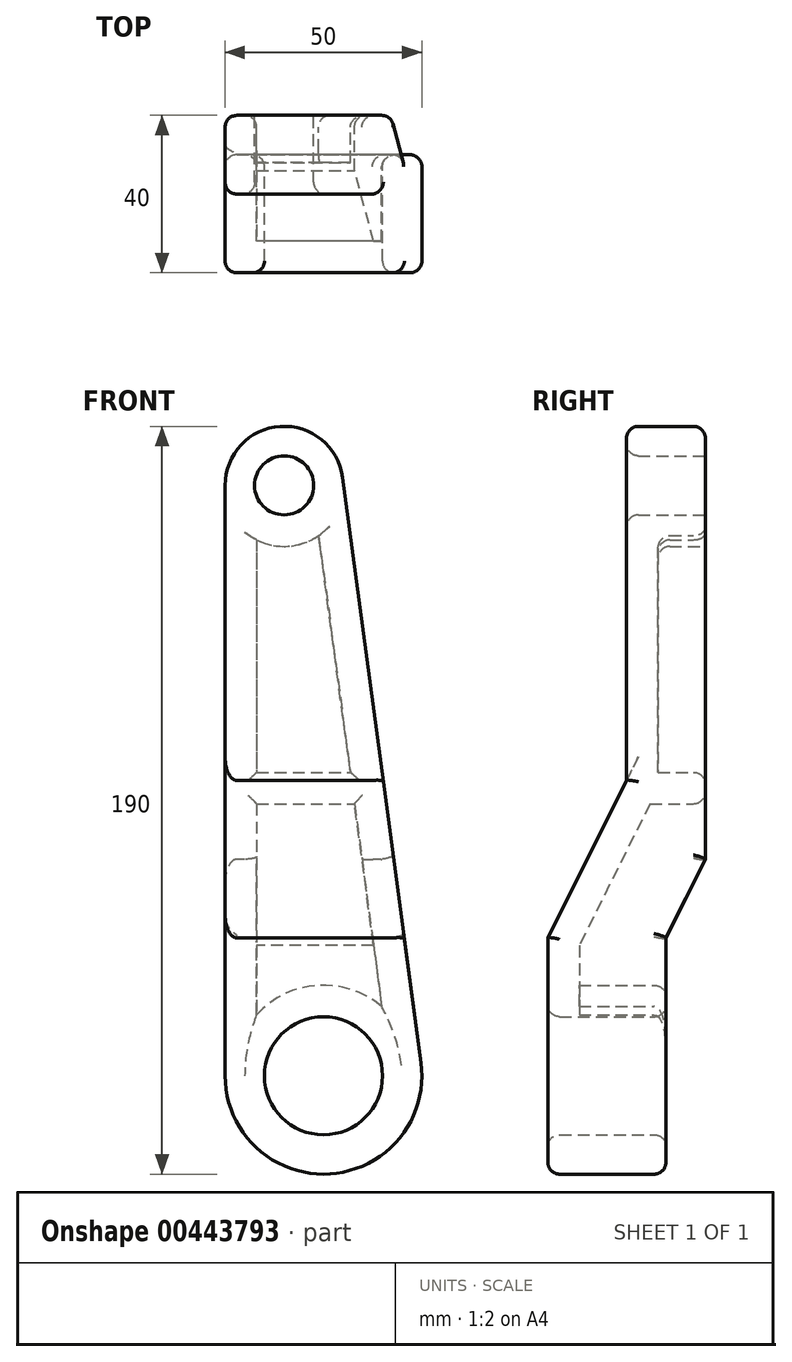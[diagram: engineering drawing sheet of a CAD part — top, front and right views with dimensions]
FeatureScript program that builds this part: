
annotation { "Feature Type Name" : "Feature", "Feature Type Description" : "" }
export const myFeature = defineFeature(function(context is Context, id is Id, definition is map)
    precondition{}
    {
        {
            var Q0;
            Q0=qCreatedBy(makeId("Front.planeOp"),FACE);
            var sketch = newSketch(context, id + "F0", { "sketchPlane" : qUnion([Q0])});
            skArc(sketch, "E0", {"start": v(-25, 0) * mm, "mid": v(1.66, -24.94) * mm, "end": v(24.78, 3.32) * mm});
            skArc(sketch, "E1", {"start": v(4.87, 152) * mm, "mid": v(-11, 164.97) * mm, "end": v(-25, 150) * mm});
            skLineSegment(sketch, "E2", {"start": v(-25, 150) * mm, "end": v(-25, 0) * mm});
            skLineSegment(sketch, "E3", {"start": v(4.87, 152) * mm, "end": v(24.78, 3.32) * mm});
            skSolve(sketch);
        }
        {
            var Q0;
            Q0 = qSketchRegion(id + "F0", true);
            extrude(context, id + "F1", {"entities" : qUnion([Q0]), "depth" : 40 * mm});
        }
        {
            var Q0;
            Q0=makeQuery(id+"F1.opExtrude","SWEPT_FACE",FACE,{"disambiguationData":[OSD([sQuery(id+"F0.wireOp",EDGE,"E2")])]});
            var sketch = newSketch(context, id + "F2", { "sketchPlane" : qUnion([Q0])});
            skLineSegment(sketch, "E4", {"start": v(0, 55) * mm, "end": v(0, -25.94) * mm});
            skLineSegment(sketch, "E5", {"start": v(10, -25.94) * mm, "end": v(10, 35) * mm});
            skLineSegment(sketch, "E6", {"start": v(10, 35) * mm, "end": v(0, 55) * mm});
            skLineSegment(sketch, "E7", {"start": v(40, 35) * mm, "end": v(40, 165.97) * mm});
            skLineSegment(sketch, "E8", {"start": v(20, 165.97) * mm, "end": v(20, 75) * mm});
            skLineSegment(sketch, "E9", {"start": v(20, 75) * mm, "end": v(40, 35) * mm});
            skLineSegment(sketch, "E10", {"start": v(0, -25.94) * mm, "end": v(10, -25.94) * mm});
            skLineSegment(sketch, "E11", {"start": v(20, 165.97) * mm, "end": v(40, 165.97) * mm});
            skSolve(sketch);
        }
        {
            var Q0;
            Q0 = qSketchRegion(id + "F2", true);
            extrude(context, id + "F3", {"entities" : qUnion([Q0]), "operationType" : NewBodyOperationType.REMOVE, "endBound" : BoundingType.THROUGH_ALL, "oppositeDirection" : true, "depth" : 25 * mm});
        }
        {
            var Q0;
            Q0=makeQuery(id+"F1.opExtrude","CAP_FACE",FACE,{"disambiguationData":[OSD([sQuery(id+"F0.wireOp",EDGE,"E0"),sQuery(id+"F0.wireOp",EDGE,"E1"),sQuery(id+"F0.wireOp",EDGE,"E2"),sQuery(id+"F0.wireOp",EDGE,"E3")])],"isStart":true});
            var sketch = newSketch(context, id + "F4", { "sketchPlane" : qUnion([Q0])});
            skCircle(sketch, "E12", {"center": v(10, 150) * mm, "radius": 7.5 * mm});
            skCircle(sketch, "E13", {"center": v(0, 0) * mm, "radius": 15 * mm});
            skSolve(sketch);
        }
        {
            var Q0;
            Q0 = qSketchRegion(id + "F4", true);
            extrude(context, id + "F5", {"entities" : qUnion([Q0]), "operationType" : NewBodyOperationType.REMOVE, "endBound" : BoundingType.THROUGH_ALL, "oppositeDirection" : true, "depth" : 25 * mm});
        }
        {
            var Q0;
            Q0=makeQuery(id+"F1.opExtrude","CAP_FACE",FACE,{"disambiguationData":[OSD([sQuery(id+"F0.wireOp",EDGE,"E0"),sQuery(id+"F0.wireOp",EDGE,"E1"),sQuery(id+"F0.wireOp",EDGE,"E2"),sQuery(id+"F0.wireOp",EDGE,"E3")])],"isStart":true});
            var Q1;
            Q1=makeQuery(id+"F3.boolean.opBoolean","COPY",FACE,{"derivedFrom":makeQuery(id+"F3.opExtrude","SWEPT_FACE",FACE,{"disambiguationData":[OSD([sQuery(id+"F2.wireOp",EDGE,"E6")])]})});
            var Q2;
            Q2=makeQuery(id+"F3.boolean.opBoolean","COPY",FACE,{"derivedFrom":makeQuery(id+"F3.opExtrude","SWEPT_FACE",FACE,{"disambiguationData":[OSD([sQuery(id+"F2.wireOp",EDGE,"E5")])]})});
            shell(context, id + "F6", {"entities" : qUnion([Q0, Q1, Q2]), "thickness" : 8 * mm});
        }
        {
            var Q0;
            Q0=makeQuery(id+"F1.opExtrude","CAP_FACE",FACE,{"disambiguationData":[OSD([sQuery(id+"F0.wireOp",EDGE,"E0"),sQuery(id+"F0.wireOp",EDGE,"E1"),sQuery(id+"F0.wireOp",EDGE,"E2"),sQuery(id+"F0.wireOp",EDGE,"E3")])],"isStart":true});
            var sketch = newSketch(context, id + "F7", { "sketchPlane" : qUnion([Q0])});
            skLineSegment(sketch, "E14", {"start": v(-6.82, 77.11) * mm, "end": v(17, 77.11) * mm});
            skLineSegment(sketch, "E15", {"start": v(-7.9, 69.11) * mm, "end": v(17, 69.11) * mm});
            skLineSegment(sketch, "E16.0", {"start": v(1.23, 137.22) * mm, "end": v(-9.79, 55) * mm});
            skLineSegment(sketch, "E17.0", {"start": v(17, 136.17) * mm, "end": v(17, 55) * mm});
            skSolve(sketch);
        }
        {
            var Q0;
            Q0 = qSketchRegion(id + "F7", true);
            extrude(context, id + "F8", {"entities" : qUnion([Q0]), "operationType" : NewBodyOperationType.ADD, "endBound" : BoundingType.UP_TO_NEXT, "oppositeDirection" : true, "depth" : 25 * mm});
        }
        {
            var Q0;
            Q0=makeQuery(id+"F3.boolean.opBoolean","INTERSECT",EDGE,{"derivedFrom":[makeQuery(id+"F1.opExtrude","SWEPT_FACE",FACE,{"disambiguationData":[OSD([sQuery(id+"F0.wireOp",EDGE,"E3")])]}),makeQuery(id+"F3.opExtrude","SWEPT_FACE",FACE,{"disambiguationData":[OSD([sQuery(id+"F2.wireOp",EDGE,"E8")])]})]});
            var Q1;
            Q1=makeQuery(id+"F1.opExtrude","CAP_EDGE",EDGE,{"disambiguationData":[OSD([sQuery(id+"F0.wireOp",EDGE,"E3")])],"isStart":true});
            var Q2;
            Q2=makeQuery(id+"F1.opExtrude","CAP_EDGE",EDGE,{"disambiguationData":[OSD([sQuery(id+"F0.wireOp",EDGE,"E1")])],"isStart":true});
            var Q3;
            Q3=makeQuery(id+"F3.boolean.opBoolean","INTERSECT",EDGE,{"derivedFrom":[makeQuery(id+"F1.opExtrude","SWEPT_FACE",FACE,{"disambiguationData":[OSD([sQuery(id+"F0.wireOp",EDGE,"E1")])]}),makeQuery(id+"F3.opExtrude","SWEPT_FACE",FACE,{"disambiguationData":[OSD([sQuery(id+"F2.wireOp",EDGE,"E8")])]})]});
            var Q4;
            Q4=makeQuery(id+"F3.boolean.opBoolean","INTERSECT",EDGE,{"derivedFrom":[makeQuery(id+"F1.opExtrude","SWEPT_FACE",FACE,{"disambiguationData":[OSD([sQuery(id+"F0.wireOp",EDGE,"E3")])]}),makeQuery(id+"F3.opExtrude","SWEPT_FACE",FACE,{"disambiguationData":[OSD([sQuery(id+"F2.wireOp",EDGE,"E9")])]})]});
            var Q5;
            Q5=makeQuery(id+"F1.opExtrude","CAP_EDGE",EDGE,{"disambiguationData":[OSD([sQuery(id+"F0.wireOp",EDGE,"E3")])],"isStart":false});
            var Q6;
            Q6=makeQuery(id+"F1.opExtrude","CAP_EDGE",EDGE,{"disambiguationData":[OSD([sQuery(id+"F0.wireOp",EDGE,"E0")])],"isStart":false});
            var Q7;
            Q7=makeQuery(id+"F1.opExtrude","CAP_EDGE",EDGE,{"disambiguationData":[OSD([sQuery(id+"F0.wireOp",EDGE,"E2")])],"isStart":false});
            var Q8;
            Q8=makeQuery(id+"F3.boolean.opBoolean","COPY",EDGE,{"derivedFrom":makeQuery(id+"F3.opExtrude","CAP_EDGE",EDGE,{"disambiguationData":[OSD([sQuery(id+"F2.wireOp",EDGE,"E9")])],"isStart":true})});
            var Q9;
            Q9=makeQuery(id+"F3.boolean.opBoolean","COPY",EDGE,{"derivedFrom":makeQuery(id+"F3.opExtrude","CAP_EDGE",EDGE,{"disambiguationData":[OSD([sQuery(id+"F2.wireOp",EDGE,"E8")])],"isStart":true})});
            var Q10;
            Q10=makeQuery(id+"F5.boolean.opBoolean","INTERSECT",EDGE,{"derivedFrom":[makeQuery(id+"F3.boolean.opBoolean","COPY",FACE,{"derivedFrom":makeQuery(id+"F3.opExtrude","SWEPT_FACE",FACE,{"disambiguationData":[OSD([sQuery(id+"F2.wireOp",EDGE,"E8")])]})}),makeQuery(id+"F5.opExtrude","SWEPT_FACE",FACE,{"disambiguationData":[OSD([sQuery(id+"F4.wireOp",EDGE,"E12")])]})]});
            var Q11;
            Q11=makeQuery(id+"F5.boolean.opBoolean","INTERSECT",EDGE,{"derivedFrom":[makeQuery(id+"F1.opExtrude","CAP_FACE",FACE,{"disambiguationData":[OSD([sQuery(id+"F0.wireOp",EDGE,"E0"),sQuery(id+"F0.wireOp",EDGE,"E1"),sQuery(id+"F0.wireOp",EDGE,"E2"),sQuery(id+"F0.wireOp",EDGE,"E3")])],"isStart":false}),makeQuery(id+"F5.opExtrude","SWEPT_FACE",FACE,{"disambiguationData":[OSD([sQuery(id+"F4.wireOp",EDGE,"E13")])]})]});
            var Q12;
            Q12=makeQuery(id+"F5.boolean.opBoolean","COPY",EDGE,{"derivedFrom":makeQuery(id+"F5.opExtrude","CAP_EDGE",EDGE,{"disambiguationData":[OSD([sQuery(id+"F4.wireOp",EDGE,"E12")])],"isStart":true})});
            var Q13;
            Q13=makeQuery(id+"F6.opShell","OFFSET_EDGE",EDGE,{"disambiguationData":[OSD([sQuery(id+"F4.wireOp",EDGE,"E12")])]});
            var Q14;
            {var subQ1=sQuery(id+"F0.wireOp",EDGE,"E3");Q14=makeQuery(id+"F8.boolean.opBoolean","SPLIT",EDGE,{"disambiguationData":[TD([makeQuery(id+"F6.opShell","OFFSET_FACE",FACE,{"disambiguationData":[OSD([sQuery(id+"F4.wireOp",EDGE,"E12")])]})])],"derivedFrom":makeQuery(id+"F6.opShell","OFFSET_EDGE",EDGE,{"disambiguationData":[OSD([subQ1]),TDD([makeQuery(id+"F1.opExtrude","CAP_EDGE",EDGE,{"disambiguationData":[OSD([subQ1])],"isStart":true})])]})});}
            var Q15;
            {var subQ1=sQuery(id+"F0.wireOp",EDGE,"E2");Q15=makeQuery(id+"F8.boolean.opBoolean","SPLIT",EDGE,{"disambiguationData":[TD([makeQuery(id+"F6.opShell","OFFSET_FACE",FACE,{"disambiguationData":[OSD([sQuery(id+"F4.wireOp",EDGE,"E12")])]})])],"derivedFrom":makeQuery(id+"F6.opShell","OFFSET_EDGE",EDGE,{"disambiguationData":[OSD([subQ1]),TDD([makeQuery(id+"F1.opExtrude","CAP_EDGE",EDGE,{"disambiguationData":[OSD([subQ1])],"isStart":true})])]})});}
            var Q16;
            Q16=makeQuery(id+"F8.opExtrude","CAP_EDGE",EDGE,{"disambiguationData":[OSD([sQuery(id+"F7.wireOp",EDGE,"E14")])],"isStart":true});
            var Q17;
            Q17=makeQuery(id+"F8.opExtrude","CAP_EDGE",EDGE,{"disambiguationData":[OSD([sQuery(id+"F7.wireOp",EDGE,"E15")])],"isStart":true});
            var Q18;
            {var subQ1=sQuery(id+"F0.wireOp",EDGE,"E3");Q18=makeQuery(id+"F8.boolean.opBoolean","SPLIT",EDGE,{"disambiguationData":[TD([makeQuery(id+"F6.opShell","OFFSET_FACE",FACE,{"disambiguationData":[OSD([sQuery(id+"F2.wireOp",EDGE,"E6")])]})])],"derivedFrom":makeQuery(id+"F6.opShell","OFFSET_EDGE",EDGE,{"disambiguationData":[OSD([subQ1]),TDD([makeQuery(id+"F1.opExtrude","CAP_EDGE",EDGE,{"disambiguationData":[OSD([subQ1])],"isStart":true})])]})});}
            var Q19;
            Q19=makeQuery(id+"F3.boolean.opBoolean","INTERSECT",EDGE,{"derivedFrom":[makeQuery(id+"F1.opExtrude","SWEPT_FACE",FACE,{"disambiguationData":[OSD([sQuery(id+"F0.wireOp",EDGE,"E3")])]}),makeQuery(id+"F3.opExtrude","SWEPT_FACE",FACE,{"disambiguationData":[OSD([sQuery(id+"F2.wireOp",EDGE,"E6")])]})]});
            var Q20;
            Q20=makeQuery(id+"F6.opShell","OFFSET_EDGE",EDGE,{"disambiguationData":[OSD([sQuery(id+"F0.wireOp",EDGE,"E3"),sQuery(id+"F2.wireOp",EDGE,"E6")])]});
            var Q21;
            {var subQ0=sQuery(id+"F0.wireOp",EDGE,"E2");Q21=makeQuery(id+"F8.boolean.opBoolean","SPLIT",EDGE,{"disambiguationData":[TD([makeQuery(id+"F3.boolean.opBoolean","COPY",FACE,{"derivedFrom":makeQuery(id+"F3.opExtrude","SWEPT_FACE",FACE,{"disambiguationData":[OSD([sQuery(id+"F2.wireOp",EDGE,"E6")])]})})])],"derivedFrom":makeQuery(id+"F6.opShell","OFFSET_EDGE",EDGE,{"disambiguationData":[OSD([subQ0]),TDD([makeQuery(id+"F1.opExtrude","CAP_EDGE",EDGE,{"disambiguationData":[OSD([subQ0])],"isStart":true})])]})});}
            var Q22;
            Q22=makeQuery(id+"F6.opShell","OFFSET_EDGE",EDGE,{"disambiguationData":[OSD([sQuery(id+"F2.wireOp",EDGE,"E6")])]});
            var Q23;
            Q23=makeQuery(id+"F6.opShell","OFFSET_EDGE",EDGE,{"disambiguationData":[OSD([sQuery(id+"F2.wireOp",EDGE,"E5")])]});
            var Q24;
            Q24=makeQuery(id+"F6.opShell","OFFSET_EDGE",EDGE,{"disambiguationData":[OSD([sQuery(id+"F0.wireOp",EDGE,"E3"),sQuery(id+"F2.wireOp",EDGE,"E5")])]});
            var Q25;
            Q25=makeQuery(id+"F3.boolean.opBoolean","INTERSECT",EDGE,{"derivedFrom":[makeQuery(id+"F1.opExtrude","SWEPT_FACE",FACE,{"disambiguationData":[OSD([sQuery(id+"F0.wireOp",EDGE,"E0")])]}),makeQuery(id+"F3.opExtrude","SWEPT_FACE",FACE,{"disambiguationData":[OSD([sQuery(id+"F2.wireOp",EDGE,"E5")])]})]});
            var Q26;
            Q26=makeQuery(id+"F6.opShell","OFFSET_EDGE",EDGE,{"disambiguationData":[OSD([sQuery(id+"F2.wireOp",EDGE,"E5"),sQuery(id+"F4.wireOp",EDGE,"E13")])]});
            var Q27;
            Q27=makeQuery(id+"F3.boolean.opBoolean","INTERSECT",EDGE,{"derivedFrom":[makeQuery(id+"F1.opExtrude","SWEPT_FACE",FACE,{"disambiguationData":[OSD([sQuery(id+"F0.wireOp",EDGE,"E3")])]}),makeQuery(id+"F3.opExtrude","SWEPT_FACE",FACE,{"disambiguationData":[OSD([sQuery(id+"F2.wireOp",EDGE,"E5")])]})]});
            var Q28;
            Q28=makeQuery(id+"F3.boolean.opBoolean","COPY",EDGE,{"derivedFrom":makeQuery(id+"F3.opExtrude","CAP_EDGE",EDGE,{"disambiguationData":[OSD([sQuery(id+"F2.wireOp",EDGE,"E5")])],"isStart":true})});
            var Q29;
            Q29=makeQuery(id+"F3.boolean.opBoolean","COPY",EDGE,{"derivedFrom":makeQuery(id+"F3.opExtrude","CAP_EDGE",EDGE,{"disambiguationData":[OSD([sQuery(id+"F2.wireOp",EDGE,"E6")])],"isStart":true})});
            var Q30;
            Q30=makeQuery(id+"F1.opExtrude","CAP_EDGE",EDGE,{"disambiguationData":[OSD([sQuery(id+"F0.wireOp",EDGE,"E2")])],"isStart":true});
            var Q31;
            Q31=makeQuery(id+"F5.boolean.opBoolean","INTERSECT",EDGE,{"derivedFrom":[makeQuery(id+"F3.boolean.opBoolean","COPY",FACE,{"derivedFrom":makeQuery(id+"F3.opExtrude","SWEPT_FACE",FACE,{"disambiguationData":[OSD([sQuery(id+"F2.wireOp",EDGE,"E5")])]})}),makeQuery(id+"F5.opExtrude","SWEPT_FACE",FACE,{"disambiguationData":[OSD([sQuery(id+"F4.wireOp",EDGE,"E13")])]})]});
            fillet(context, id + "F9", {"entities" : qUnion([Q0, Q1, Q2, Q3, Q4, Q5, Q6, Q7, Q8, Q9, Q10, Q11, Q12, Q13, Q14, Q15, Q16, Q17, Q18, Q19, Q20, Q21, Q22, Q23, Q24, Q25, Q26, Q27, Q28, Q29, Q30, Q31]), "radius" : 3 * mm, "tangentPropagation" : true, "allowEdgeOverflow" : false});
        }
    });
